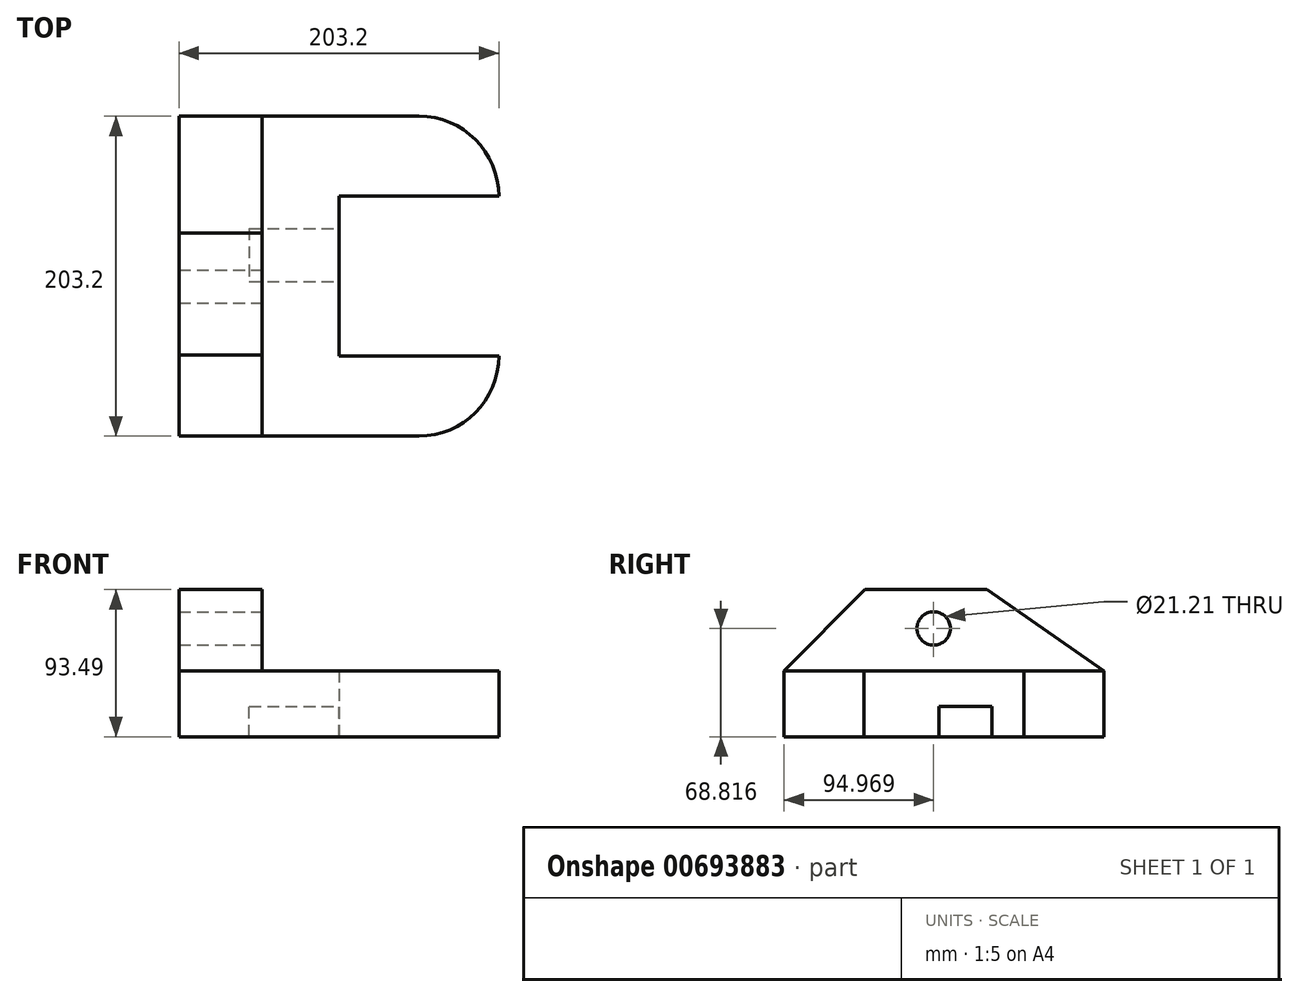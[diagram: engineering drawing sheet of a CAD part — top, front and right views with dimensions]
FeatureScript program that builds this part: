
annotation { "Feature Type Name" : "Feature", "Feature Type Description" : "" }
export const myFeature = defineFeature(function(context is Context, id is Id, definition is map)
    precondition{}
    {
        {
            var Q0;
            Q0=qCreatedBy(makeId("Top.planeOp"),FACE);
            var sketch = newSketch(context, id + "F0", { "sketchPlane" : qUnion([Q0])});
            skLineSegment(sketch, "E0", {"start": v(0, -101.6) * mm, "end": v(0, 101.6) * mm});
            skLineSegment(sketch, "E1", {"start": v(0, 101.6) * mm, "end": v(152.4, 101.6) * mm});
            skLineSegment(sketch, "E2", {"start": v(0, -101.6) * mm, "end": v(152.4, -101.6) * mm});
            skArc(sketch, "E3", {"start": v(152.4, -101.6) * mm, "mid": v(188.32, -86.72) * mm, "end": v(203.2, -50.8) * mm});
            skArc(sketch, "E4", {"start": v(203.2, 50.8) * mm, "mid": v(188.32, 86.72) * mm, "end": v(152.4, 101.6) * mm});
            skLineSegment(sketch, "E5", {"start": v(101.6, 50.8) * mm, "end": v(101.6, -50.8) * mm});
            skLineSegment(sketch, "E6", {"start": v(101.6, -50.8) * mm, "end": v(203.2, -50.8) * mm});
            skLineSegment(sketch, "E7", {"start": v(101.6, 50.8) * mm, "end": v(203.2, 50.8) * mm});
            skSolve(sketch);
        }
        {
            var Q0;
            Q0=makeQuery(id+"F0.imprint","IMPRINT",FACE,{"disambiguationData":[TD([[makeQuery(id+"F0.imprint","IMPRINT",EDGE,{"derivedFrom":sQuery(id+"F0.wireOp",EDGE,"E0")}),-1.0]])]});
            extrude(context, id + "F1", {"entities" : qUnion([Q0]), "depth" : 41.9 * mm, "offsetDistance" : 25.4 * mm});
        }
        {
            var Q0;
            Q0=makeQuery(id+"F1.opExtrude","SWEPT_FACE",FACE,{"disambiguationData":[OSD([sQuery(id+"F0.wireOp",EDGE,"E0")])]});
            var sketch = newSketch(context, id + "F2", { "sketchPlane" : qUnion([Q0])});
            skLineSegment(sketch, "E8", {"start": v(-101.6, 41.9) * mm, "end": v(-27.38, 93.5) * mm});
            skLineSegment(sketch, "E9", {"start": v(-27.38, 93.5) * mm, "end": v(50.25, 93.5) * mm});
            skLineSegment(sketch, "E10", {"start": v(50.25, 93.5) * mm, "end": v(101.6, 41.91) * mm});
            skSolve(sketch);
        }
        {
            var Q0;
            Q0=makeQuery(id+"F2.imprint","IMPRINT",FACE,{"disambiguationData":[TD([[makeQuery(id+"F2.imprint","IMPRINT",EDGE,{"derivedFrom":sQuery(id+"F2.wireOp",EDGE,"E8")}),-1.0]])]});
            extrude(context, id + "F3", {"entities" : qUnion([Q0]), "operationType" : NewBodyOperationType.ADD, "oppositeDirection" : true, "depth" : 52.83 * mm, "offsetDistance" : 25.4 * mm});
        }
        {
            var Q0;
            Q0=makeQuery(id+"F3.opExtrude","CAP_FACE",FACE,{"disambiguationData":[OSD([sQuery(id+"F0.wireOp",EDGE,"E0"),sQuery(id+"F2.wireOp",EDGE,"E8"),sQuery(id+"F2.wireOp",EDGE,"E9"),sQuery(id+"F2.wireOp",EDGE,"E10")])],"isStart":false});
            var sketch = newSketch(context, id + "F4", { "sketchPlane" : qUnion([Q0])});
            skCircle(sketch, "E11", {"center": v(-6.63, 68.82) * mm, "radius": 10.6 * mm});
            skSolve(sketch);
        }
        {
            var Q0;
            Q0=makeQuery(id+"F4.imprint","IMPRINT",FACE,{"disambiguationData":[TD([[makeQuery(id+"F4.imprint","IMPRINT",EDGE,{"derivedFrom":sQuery(id+"F4.wireOp",EDGE,"E11")}),1.0]])]});
            extrude(context, id + "F5", {"entities" : qUnion([Q0]), "operationType" : NewBodyOperationType.REMOVE, "oppositeDirection" : true, "depth" : 85.6 * mm, "offsetDistance" : 25.4 * mm});
        }
        {
            var Q0;
            Q0=makeQuery(id+"F1.opExtrude","SWEPT_FACE",FACE,{"disambiguationData":[OSD([sQuery(id+"F0.wireOp",EDGE,"E5")])]});
            var sketch = newSketch(context, id + "F6", { "sketchPlane" : qUnion([Q0])});
            skLineSegment(sketch, "E12", {"start": v(30.32, 0) * mm, "end": v(30.32, 19.18) * mm});
            skLineSegment(sketch, "E13", {"start": v(30.32, 19.18) * mm, "end": v(-3.4, 19.18) * mm});
            skLineSegment(sketch, "E14", {"start": v(-3.4, 19.18) * mm, "end": v(-3.4, 0) * mm});
            skSolve(sketch);
        }
        {
            var Q0;
            {var subQ0=sQuery(id+"F6.wireOp",EDGE,"E12");Q0=makeQuery(id+"F6.imprint","IMPRINT",FACE,{"disambiguationData":[TD([[makeQuery(id+"F6.imprint","IMPRINT",EDGE,{"derivedFrom":subQ0}),1.0]])]});}
            extrude(context, id + "F7", {"entities" : qUnion([Q0]), "operationType" : NewBodyOperationType.REMOVE, "oppositeDirection" : true, "depth" : 56.9 * mm, "offsetDistance" : 25.4 * mm});
        }
    });
